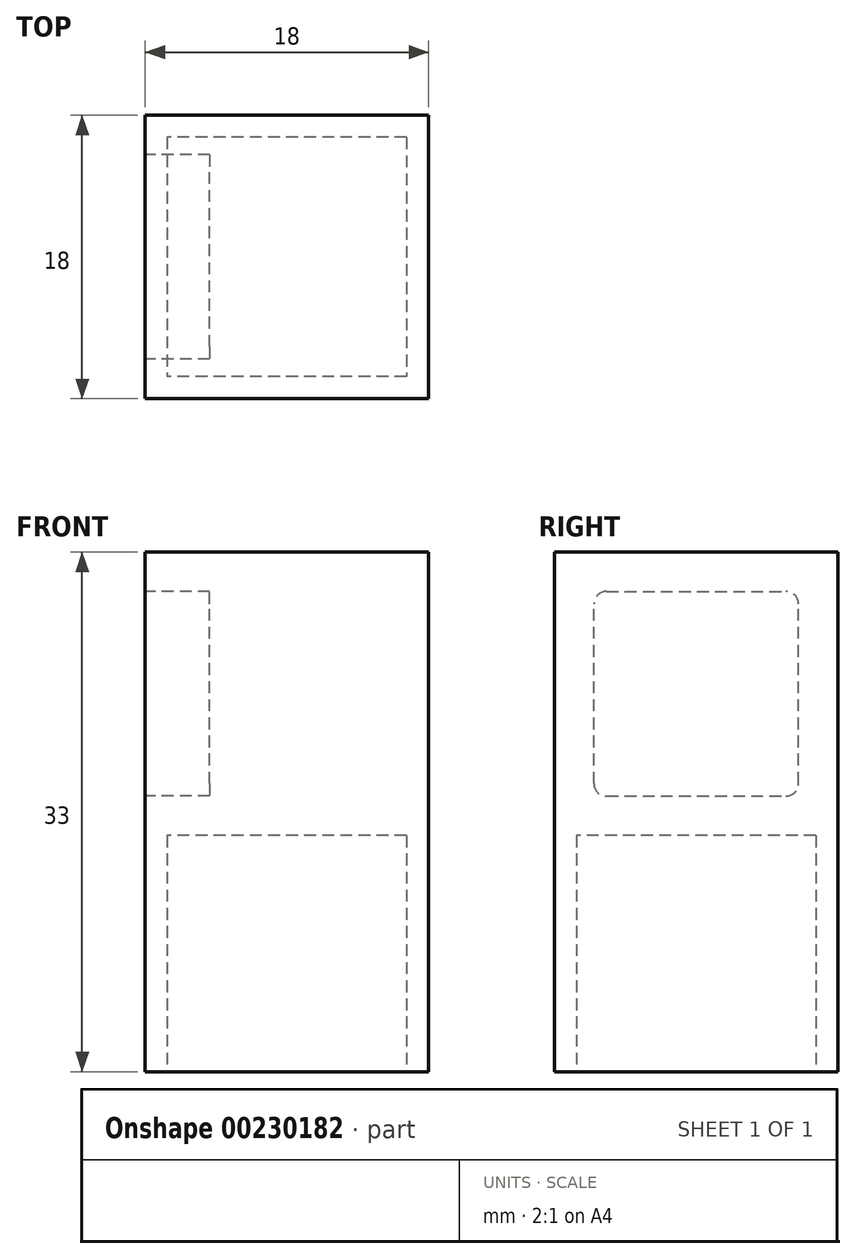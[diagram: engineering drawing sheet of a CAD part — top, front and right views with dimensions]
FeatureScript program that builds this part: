
annotation { "Feature Type Name" : "Feature", "Feature Type Description" : "" }
export const myFeature = defineFeature(function(context is Context, id is Id, definition is map)
    precondition{}
    {
        {
            var Q0;
            Q0=qCreatedBy(makeId("Top.planeOp"),FACE);
            var sketch = newSketch(context, id + "F0", { "sketchPlane" : qUnion([Q0])});
            skLineSegment(sketch, "E0.bottom", {"start": v(9, -9) * mm, "end": v(-9, -9) * mm});
            skLineSegment(sketch, "E0.top", {"start": v(9, 9) * mm, "end": v(-9, 9) * mm});
            skLineSegment(sketch, "E0.left", {"start": v(9, -9) * mm, "end": v(9, 9) * mm});
            skLineSegment(sketch, "E0.right", {"start": v(-9, -9) * mm, "end": v(-9, 9) * mm});
            skPoint(sketch, "E0.middle", {"position": v(0, 0) * mm});
            skSolve(sketch);
        }
        {
            var Q0;
            Q0 = qSketchRegion(id + "F0", true);
            extrude(context, id + "F1", {"entities" : qUnion([Q0]), "depth" : 25 * mm});
        }
        {
            var Q0;
            Q0=makeQuery(id+"F1.opExtrude","CAP_FACE",FACE,{"disambiguationData":[OSD([sQuery(id+"F0.wireOp",EDGE,"E0.bottom"),sQuery(id+"F0.wireOp",EDGE,"E0.top"),sQuery(id+"F0.wireOp",EDGE,"E0.left"),sQuery(id+"F0.wireOp",EDGE,"E0.right")])],"isStart":false});
            extrude(context, id + "F2", {"entities" : qUnion([Q0]), "operationType" : NewBodyOperationType.ADD, "depth" : 8 * mm});
        }
        {
            var Q0;
            {var subQ0=sQuery(id+"F0.wireOp",EDGE,"E0.right");Q0=makeQuery(id+"F2.boolean.opBoolean","MERGE",FACE,{"derivedFrom":[makeQuery(id+"F1.opExtrude","SWEPT_FACE",FACE,{"disambiguationData":[OSD([subQ0])]}),makeQuery(id+"F2.opExtrude","SWEPT_FACE",FACE,{"disambiguationData":[OSD([subQ0])]})]});}
            var sketch = newSketch(context, id + "F3", { "sketchPlane" : qUnion([Q0])});
            skLineSegment(sketch, "E1", {"start": v(0, 33) * mm, "end": v(0, 15) * mm});
            skPoint(sketch, "E1.endSnap0", {"position": v(0, 33) * mm});
            skLineSegment(sketch, "E2.bottom", {"start": v(6.5, 17.5) * mm, "end": v(-6.5, 17.5) * mm});
            skLineSegment(sketch, "E2.top", {"start": v(6.5, 30.5) * mm, "end": v(-6.5, 30.5) * mm});
            skLineSegment(sketch, "E2.left", {"start": v(6.5, 17.5) * mm, "end": v(6.5, 30.5) * mm});
            skLineSegment(sketch, "E2.right", {"start": v(-6.5, 17.5) * mm, "end": v(-6.5, 30.5) * mm});
            skPoint(sketch, "E2.middle", {"position": v(0, 24) * mm});
            skSolve(sketch);
        }
        {
            var Q0;
            Q0 = qSketchRegion(id + "F3", true);
            extrude(context, id + "F4", {"entities" : qUnion([Q0]), "operationType" : NewBodyOperationType.REMOVE, "oppositeDirection" : true, "depth" : 4.1 * mm});
        }
        {
            var Q0;
            Q0=makeQuery(id+"F1.opExtrude","CAP_FACE",FACE,{"disambiguationData":[OSD([sQuery(id+"F0.wireOp",EDGE,"E0.bottom"),sQuery(id+"F0.wireOp",EDGE,"E0.top"),sQuery(id+"F0.wireOp",EDGE,"E0.left"),sQuery(id+"F0.wireOp",EDGE,"E0.right")])],"isStart":true});
            var sketch = newSketch(context, id + "F5", { "sketchPlane" : qUnion([Q0])});
            skLineSegment(sketch, "E3.bottom", {"start": v(7.6, -7.6) * mm, "end": v(-7.6, -7.6) * mm});
            skLineSegment(sketch, "E3.top", {"start": v(7.6, 7.6) * mm, "end": v(-7.6, 7.6) * mm});
            skLineSegment(sketch, "E3.left", {"start": v(7.6, -7.6) * mm, "end": v(7.6, 7.6) * mm});
            skLineSegment(sketch, "E3.right", {"start": v(-7.6, -7.6) * mm, "end": v(-7.6, 7.6) * mm});
            skPoint(sketch, "E3.middle", {"position": v(0, 0) * mm});
            skSolve(sketch);
        }
        {
            var Q0;
            Q0 = qSketchRegion(id + "F5", true);
            extrude(context, id + "F6", {"entities" : qUnion([Q0]), "operationType" : NewBodyOperationType.REMOVE, "oppositeDirection" : true, "depth" : 15 * mm});
        }
        {
            var Q0;
            Q0=makeQuery(id+"F4.boolean.opBoolean","COPY",EDGE,{"derivedFrom":makeQuery(id+"F4.opExtrude","SWEPT_EDGE",EDGE,{"disambiguationData":[OSD([sQuery(id+"F3.wireOp",EDGE,"E2.top"),sQuery(id+"F3.wireOp",EDGE,"E2.right")])]})});
            var Q1;
            Q1=makeQuery(id+"F4.boolean.opBoolean","COPY",EDGE,{"derivedFrom":makeQuery(id+"F4.opExtrude","SWEPT_EDGE",EDGE,{"disambiguationData":[OSD([sQuery(id+"F3.wireOp",EDGE,"E2.top"),sQuery(id+"F3.wireOp",EDGE,"E2.left")])]})});
            var Q2;
            Q2=makeQuery(id+"F4.boolean.opBoolean","COPY",EDGE,{"derivedFrom":makeQuery(id+"F4.opExtrude","SWEPT_EDGE",EDGE,{"disambiguationData":[OSD([sQuery(id+"F3.wireOp",EDGE,"E2.bottom"),sQuery(id+"F3.wireOp",EDGE,"E2.left")])]})});
            var Q3;
            Q3=makeQuery(id+"F4.boolean.opBoolean","COPY",EDGE,{"derivedFrom":makeQuery(id+"F4.opExtrude","SWEPT_EDGE",EDGE,{"disambiguationData":[OSD([sQuery(id+"F3.wireOp",EDGE,"E2.bottom"),sQuery(id+"F3.wireOp",EDGE,"E2.right")])]})});
            fillet(context, id + "F7", {"entities" : qUnion([Q0, Q1, Q2, Q3]), "radius" : 0.8 * mm, "tangentPropagation" : true, "allowEdgeOverflow" : false});
        }
    });
